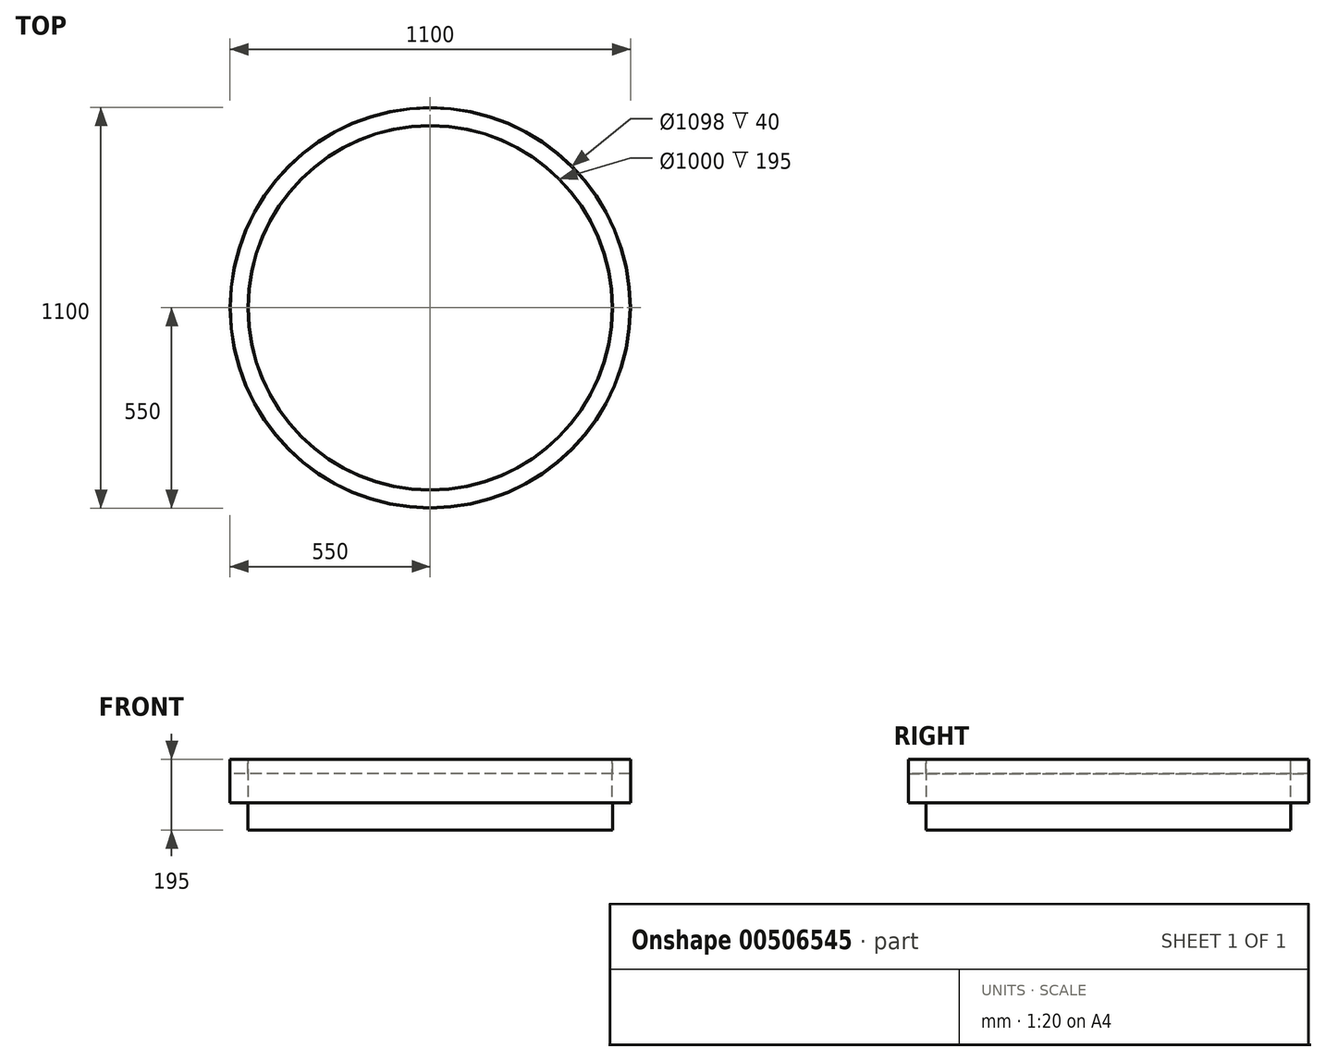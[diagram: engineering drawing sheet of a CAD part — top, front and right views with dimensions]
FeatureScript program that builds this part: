
annotation { "Feature Type Name" : "Feature", "Feature Type Description" : "" }
export const myFeature = defineFeature(function(context is Context, id is Id, definition is map)
    precondition{}
    {
        {
            var Q0;
            Q0=qCreatedBy(makeId("Front.planeOp"),FACE);
            var sketch = newSketch(context, id + "F0", { "sketchPlane" : qUnion([Q0])});
            skLineSegment(sketch, "E0", {"start": v(0, 710.75) * mm, "end": v(0, -704.58) * mm, "construction": true});
            skLineSegment(sketch, "E1", {"start": v(-500, 215.65) * mm, "end": v(-500, 410.65) * mm});
            skLineSegment(sketch, "E2", {"start": v(-500, 410.65) * mm, "end": v(-501, 410.65) * mm});
            skLineSegment(sketch, "E3", {"start": v(-549, 410.65) * mm, "end": v(-550, 410.65) * mm});
            skLineSegment(sketch, "E4", {"start": v(-550, 410.65) * mm, "end": v(-550, 290.65) * mm});
            skLineSegment(sketch, "E5", {"start": v(-550, 290.65) * mm, "end": v(-501, 290.65) * mm});
            skLineSegment(sketch, "E6", {"start": v(-501, 290.65) * mm, "end": v(-501, 215.65) * mm});
            skLineSegment(sketch, "E7", {"start": v(-549, 410.65) * mm, "end": v(-549, 370.65) * mm});
            skLineSegment(sketch, "E8", {"start": v(-549, 370.65) * mm, "end": v(-501, 370.65) * mm});
            skLineSegment(sketch, "E9", {"start": v(-501, 370.65) * mm, "end": v(-501, 410.65) * mm});
            skLineSegment(sketch, "E10", {"start": v(-501, 215.65) * mm, "end": v(-500, 215.65) * mm});
            skSolve(sketch);
        }
        {
            var Q0;
            Q0=qSketchRegion(id+"F0",true);
            var Q1;
            Q1=sQuery(id+"F0.wireOp",EDGE,"E0");
            revolve(context, id + "F1", {"entities" : qUnion([Q0]), "axis" : qUnion([Q1]), "revolveType" : RevolveType.FULL});
        }
    });
